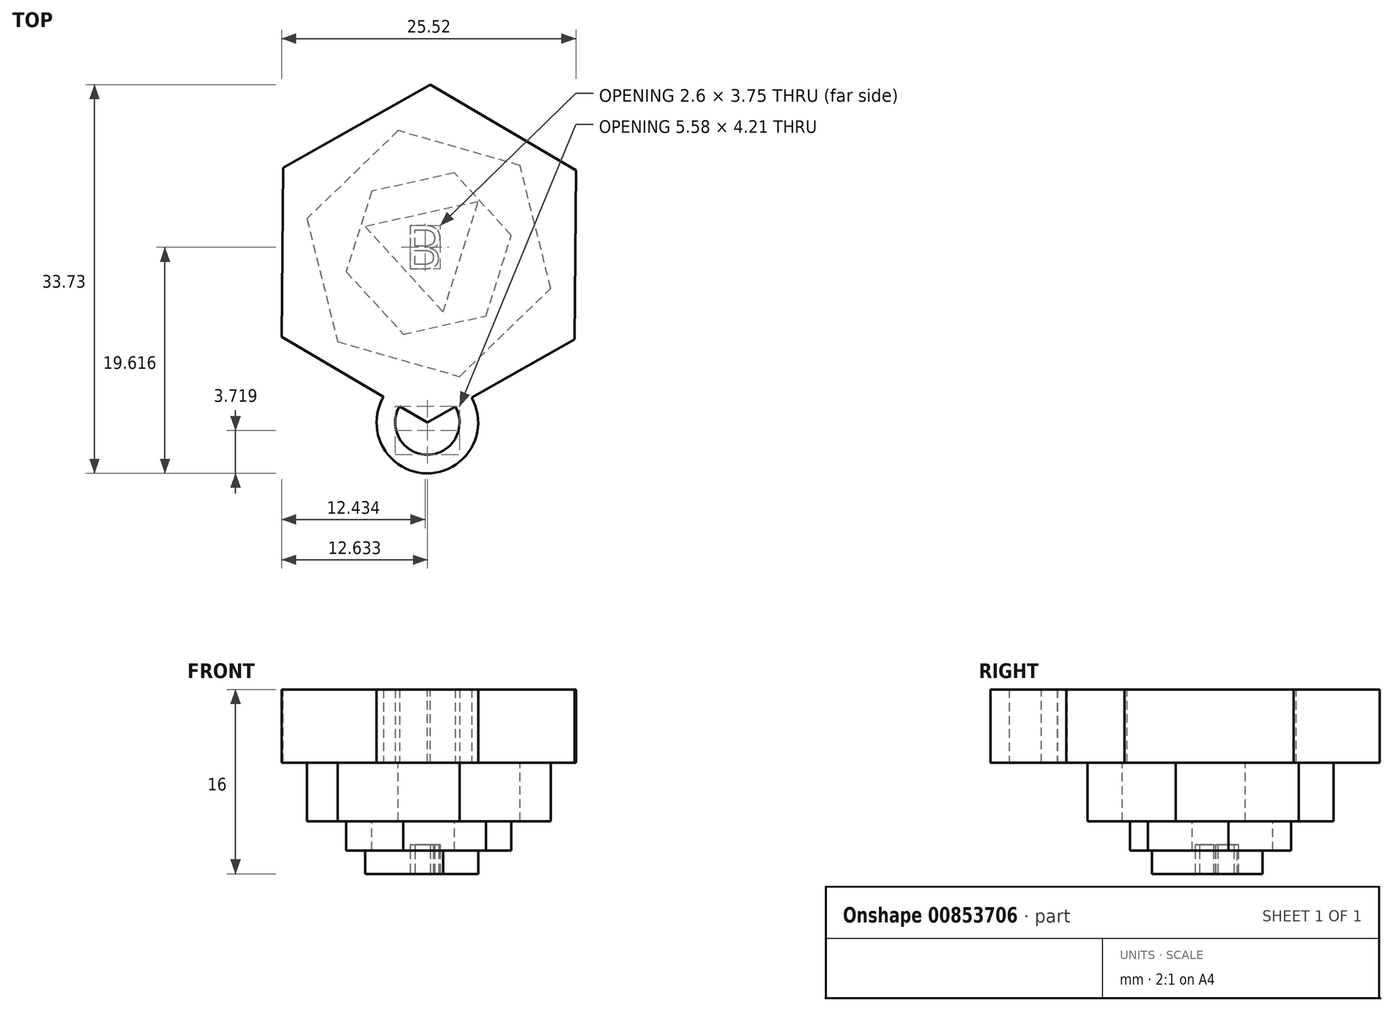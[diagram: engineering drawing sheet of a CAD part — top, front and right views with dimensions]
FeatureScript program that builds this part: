
annotation { "Feature Type Name" : "Feature", "Feature Type Description" : "" }
export const myFeature = defineFeature(function(context is Context, id is Id, definition is map)
    precondition{}
    {
        {
            var Q0;
            Q0=qCreatedBy(makeId("Top.planeOp"),FACE);
            var sketch = newSketch(context, id + "F0", { "sketchPlane" : qUnion([Q0])});
            skCircle(sketch, "E0.cCircle", {"center": v(0, 0) * mm, "radius": 12.7 * mm, "construction": true});
            skLineSegment(sketch, "E0.0", {"start": v(12.64, -7.44) * mm, "end": v(-0.13, -14.66) * mm});
            skLineSegment(sketch, "E0.1", {"start": v(-0.13, -14.66) * mm, "end": v(-12.76, -7.22) * mm});
            skLineSegment(sketch, "E0.2", {"start": v(-12.76, -7.22) * mm, "end": v(-12.64, 7.44) * mm});
            skLineSegment(sketch, "E0.3", {"start": v(-12.64, 7.44) * mm, "end": v(0.13, 14.66) * mm});
            skLineSegment(sketch, "E0.4", {"start": v(0.13, 14.66) * mm, "end": v(12.76, 7.22) * mm});
            skLineSegment(sketch, "E0.5", {"start": v(12.76, 7.22) * mm, "end": v(12.64, -7.44) * mm});
            skPoint(sketch, "E0.0.midPoint", {"position": v(6.25, -11.05) * mm});
            skPoint(sketch, "E1.0.midPoint", {"position": v(2.58, 10.3) * mm});
            skSolve(sketch);
        }
        {
            var Q0;
            Q0=makeQuery(id+"F0.imprint","IMPRINT",FACE,{"disambiguationData":[TD([[makeQuery(id+"F0.imprint","IMPRINT",EDGE,{"derivedFrom":sQuery(id+"F0.wireOp",EDGE,"E0.0")}),-1.0]])]});
            extrude(context, id + "F1", {"entities" : qUnion([Q0]), "oppositeDirection" : true, "depth" : 6.35 * mm, "offsetDistance" : 25.4 * mm});
        }
        {
            var Q0;
            Q0=makeQuery(id+"F1.opExtrude","CAP_FACE",FACE,{"disambiguationData":[OSD([sQuery(id+"F0.wireOp",EDGE,"E0.0"),sQuery(id+"F0.wireOp",EDGE,"E0.1"),sQuery(id+"F0.wireOp",EDGE,"E0.2"),sQuery(id+"F0.wireOp",EDGE,"E0.3"),sQuery(id+"F0.wireOp",EDGE,"E0.4"),sQuery(id+"F0.wireOp",EDGE,"E0.5")])],"isStart":false});
            var sketch = newSketch(context, id + "F2", { "sketchPlane" : qUnion([Q0])});
            skCircle(sketch, "E2.cCircle", {"center": v(0, 0) * mm, "radius": 9.53 * mm, "construction": true});
            skLineSegment(sketch, "E2.0", {"start": v(7.9, -7.65) * mm, "end": v(-2.67, -10.67) * mm});
            skLineSegment(sketch, "E2.1", {"start": v(-2.67, -10.67) * mm, "end": v(-10.58, -3.02) * mm});
            skLineSegment(sketch, "E2.2", {"start": v(-10.58, -3.02) * mm, "end": v(-7.9, 7.65) * mm});
            skLineSegment(sketch, "E2.3", {"start": v(-7.9, 7.65) * mm, "end": v(2.67, 10.67) * mm});
            skLineSegment(sketch, "E2.4", {"start": v(2.67, 10.67) * mm, "end": v(10.58, 3.02) * mm});
            skLineSegment(sketch, "E2.5", {"start": v(10.58, 3.02) * mm, "end": v(7.9, -7.65) * mm});
            skPoint(sketch, "E2.0.midPoint", {"position": v(2.61, -9.16) * mm});
            skSolve(sketch);
        }
        {
            var Q0;
            Q0=makeQuery(id+"F2.imprint","IMPRINT",FACE,{"disambiguationData":[TD([[makeQuery(id+"F2.imprint","IMPRINT",EDGE,{"derivedFrom":sQuery(id+"F2.wireOp",EDGE,"E2.0")}),-1.0]])]});
            extrude(context, id + "F3", {"entities" : qUnion([Q0]), "depth" : 5.08 * mm, "offsetDistance" : 25.4 * mm});
        }
        {
            var Q0;
            Q0=makeQuery(id+"F3.opExtrude","CAP_FACE",FACE,{"disambiguationData":[OSD([sQuery(id+"F2.wireOp",EDGE,"E2.0"),sQuery(id+"F2.wireOp",EDGE,"E2.1"),sQuery(id+"F2.wireOp",EDGE,"E2.2"),sQuery(id+"F2.wireOp",EDGE,"E2.3"),sQuery(id+"F2.wireOp",EDGE,"E2.4"),sQuery(id+"F2.wireOp",EDGE,"E2.5")])],"isStart":false});
            var sketch = newSketch(context, id + "F4", { "sketchPlane" : qUnion([Q0])});
            skCircle(sketch, "E3.cCircle", {"center": v(0, 0) * mm, "radius": 6.35 * mm, "construction": true});
            skLineSegment(sketch, "E3.0", {"start": v(7.16, -1.58) * mm, "end": v(2.21, -7) * mm});
            skLineSegment(sketch, "E3.1", {"start": v(2.21, -7) * mm, "end": v(-4.95, -5.41) * mm});
            skLineSegment(sketch, "E3.2", {"start": v(-4.95, -5.41) * mm, "end": v(-7.16, 1.58) * mm});
            skLineSegment(sketch, "E3.3", {"start": v(-7.16, 1.58) * mm, "end": v(-2.21, 7) * mm});
            skLineSegment(sketch, "E3.4", {"start": v(-2.21, 7) * mm, "end": v(4.95, 5.41) * mm});
            skLineSegment(sketch, "E3.5", {"start": v(4.95, 5.41) * mm, "end": v(7.16, -1.58) * mm});
            skPoint(sketch, "E3.0.midPoint", {"position": v(4.69, -4.29) * mm});
            skSolve(sketch);
        }
        {
            var Q0;
            Q0=makeQuery(id+"F4.imprint","IMPRINT",FACE,{"disambiguationData":[TD([[makeQuery(id+"F4.imprint","IMPRINT",EDGE,{"derivedFrom":sQuery(id+"F4.wireOp",EDGE,"E3.0")}),-1.0]])]});
            extrude(context, id + "F5", {"entities" : qUnion([Q0]), "operationType" : NewBodyOperationType.ADD, "depth" : 2.54 * mm, "offsetDistance" : 25.4 * mm});
        }
        {
            var Q0;
            Q0=makeQuery(id+"F5.opExtrude","CAP_FACE",FACE,{"disambiguationData":[OSD([sQuery(id+"F4.wireOp",EDGE,"E3.0"),sQuery(id+"F4.wireOp",EDGE,"E3.1"),sQuery(id+"F4.wireOp",EDGE,"E3.2"),sQuery(id+"F4.wireOp",EDGE,"E3.3"),sQuery(id+"F4.wireOp",EDGE,"E3.4"),sQuery(id+"F4.wireOp",EDGE,"E3.5")])],"isStart":false});
            var sketch = newSketch(context, id + "F6", { "sketchPlane" : qUnion([Q0])});
            skCircle(sketch, "E4.cCircle", {"center": v(0, -0.6) * mm, "radius": 2.9 * mm, "construction": true});
            skLineSegment(sketch, "E4.0", {"start": v(-5.53, -2.34) * mm, "end": v(1.25, 5.07) * mm});
            skLineSegment(sketch, "E4.1", {"start": v(1.25, 5.07) * mm, "end": v(4.28, -4.5) * mm});
            skLineSegment(sketch, "E4.2", {"start": v(4.28, -4.5) * mm, "end": v(-5.53, -2.34) * mm});
            skPoint(sketch, "E4.0.midPoint", {"position": v(-2.14, 1.37) * mm});
            skSolve(sketch);
        }
        {
            var Q0;
            Q0=makeQuery(id+"F6.imprint","IMPRINT",FACE,{"disambiguationData":[TD([[makeQuery(id+"F6.imprint","IMPRINT",EDGE,{"derivedFrom":sQuery(id+"F6.wireOp",EDGE,"E4.0")}),-1.0]])]});
            extrude(context, id + "F7", {"entities" : qUnion([Q0]), "depth" : 2.03 * mm, "offsetDistance" : 25.4 * mm});
        }
        {
            var Q0;
            Q0=makeQuery(id+"F7.opExtrude","CAP_FACE",FACE,{"disambiguationData":[OSD([sQuery(id+"F6.wireOp",EDGE,"E4.0"),sQuery(id+"F6.wireOp",EDGE,"E4.1"),sQuery(id+"F6.wireOp",EDGE,"E4.2")])],"isStart":false});
            var sketch = newSketch(context, id + "F8", { "sketchPlane" : qUnion([Q0])});
            skText(sketch, "E5", { "text": "B", "fontName": "OpenSans-Regular.ttf"});
            const initialGuessF8  = {"E5": [-0.00214, -0.00242, 1, 0, 0.00378]};
            skSetInitialGuess(sketch, initialGuessF8);
            skSolve(sketch);
        }
        {
            var Q0;
            Q0 = qSketchRegion(id + "F8", true);
            extrude(context, id + "F9", {"entities" : qUnion([Q0]), "operationType" : NewBodyOperationType.REMOVE, "oppositeDirection" : true, "depth" : 2.54 * mm, "offsetDistance" : 25.4 * mm});
        }
        {
            var Q0;
            Q0=makeQuery(id+"F1.opExtrude","CAP_FACE",FACE,{"disambiguationData":[OSD([sQuery(id+"F0.wireOp",EDGE,"E0.0"),sQuery(id+"F0.wireOp",EDGE,"E0.1"),sQuery(id+"F0.wireOp",EDGE,"E0.2"),sQuery(id+"F0.wireOp",EDGE,"E0.3"),sQuery(id+"F0.wireOp",EDGE,"E0.4"),sQuery(id+"F0.wireOp",EDGE,"E0.5")])],"isStart":false});
            var sketch = newSketch(context, id + "F10", { "sketchPlane" : qUnion([Q0])});
            skCircle(sketch, "E6", {"center": v(-0.13, 14.66) * mm, "radius": 4.4 * mm});
            skCircle(sketch, "E7", {"center": v(-0.13, 14.66) * mm, "radius": 2.8 * mm});
            skSolve(sketch);
        }
        {
            var Q0;
            {var subQ0=sQuery(id+"F10.wireOp",EDGE,"E6");var subQ1=makeQuery(id+"F1.opExtrude","CAP_EDGE",EDGE,{"disambiguationData":[OSD([sQuery(id+"F0.wireOp",EDGE,"E0.0")])],"isStart":false});var subQ2=makeQuery(id+"F10.imprint","INTERSECT",VERTEX,{"derivedFrom":[subQ1,subQ0]});Q0=makeQuery(id+"F10.imprint","IMPRINT",FACE,{"disambiguationData":[TD([[makeQuery(id+"F10.imprint","IMPRINT",EDGE,{"disambiguationData":[TD([[subQ2,-1.0]])],"derivedFrom":subQ0}),1.0]])]});}
            var Q1;
            Q1=makeQuery(id+"F1.opExtrude","CAP_FACE",FACE,{"disambiguationData":[OSD([sQuery(id+"F0.wireOp",EDGE,"E0.0"),sQuery(id+"F0.wireOp",EDGE,"E0.1"),sQuery(id+"F0.wireOp",EDGE,"E0.2"),sQuery(id+"F0.wireOp",EDGE,"E0.3"),sQuery(id+"F0.wireOp",EDGE,"E0.4"),sQuery(id+"F0.wireOp",EDGE,"E0.5")])],"isStart":false});
            extrude(context, id + "F11", {"entities" : qUnion([Q0]), "operationType" : NewBodyOperationType.ADD, "oppositeDirection" : true, "depth" : 6.35 * mm, "endBoundEntityFace" : qUnion([Q1]), "offsetDistance" : 25.4 * mm});
        }
    });
